# Revit family: Door_Entry_FL-400-SHAKE-IT-UP_Cross-Aluminum
name_source: partatom
category: Doors
units: mm (PartAtom-declared; Revit-internal decimal feet)

## family parameters
Always vertical = Yes
Classification Number = 23.30.10.00
Cut with Voids When Loaded = No
Host = Wall
Room Calculation Point = No
Shared = No

## types (1)
- FL-400-SHAKE IT UP
    Analytic Construction = <None>
    Description = Flush Aluminum Commercial Doors - FL-400
    Door Panel Width = 2' - 6"
    Frame Material = Aluminum
    Function = Interior
    Glass Material = Glass Material
    H1 = 7' - 0"
    Height = 7' - 0"
    Keynote = 08 11 00
    Manufacturer = Cross Aluminum
    Model = FL-400-SHAKE IT UP
    Product Documentation Link = https://www.arcat.com
    Product Page URL = https://www.arcat.com
    Rough Height = 7' - 0"
    Rough Width = 5' - 0"
    Thickness = 0' - 0"
    URL = https://www.crossaluminum.com
    W1 = 5' - 0"
    Wall Closure = By host
    Width = 6' - 0"
    Window Width = 1' - 0"

## geometry (parser evidence)
native form markers: Sweep x13
no freeform markers — native parametric forms only
